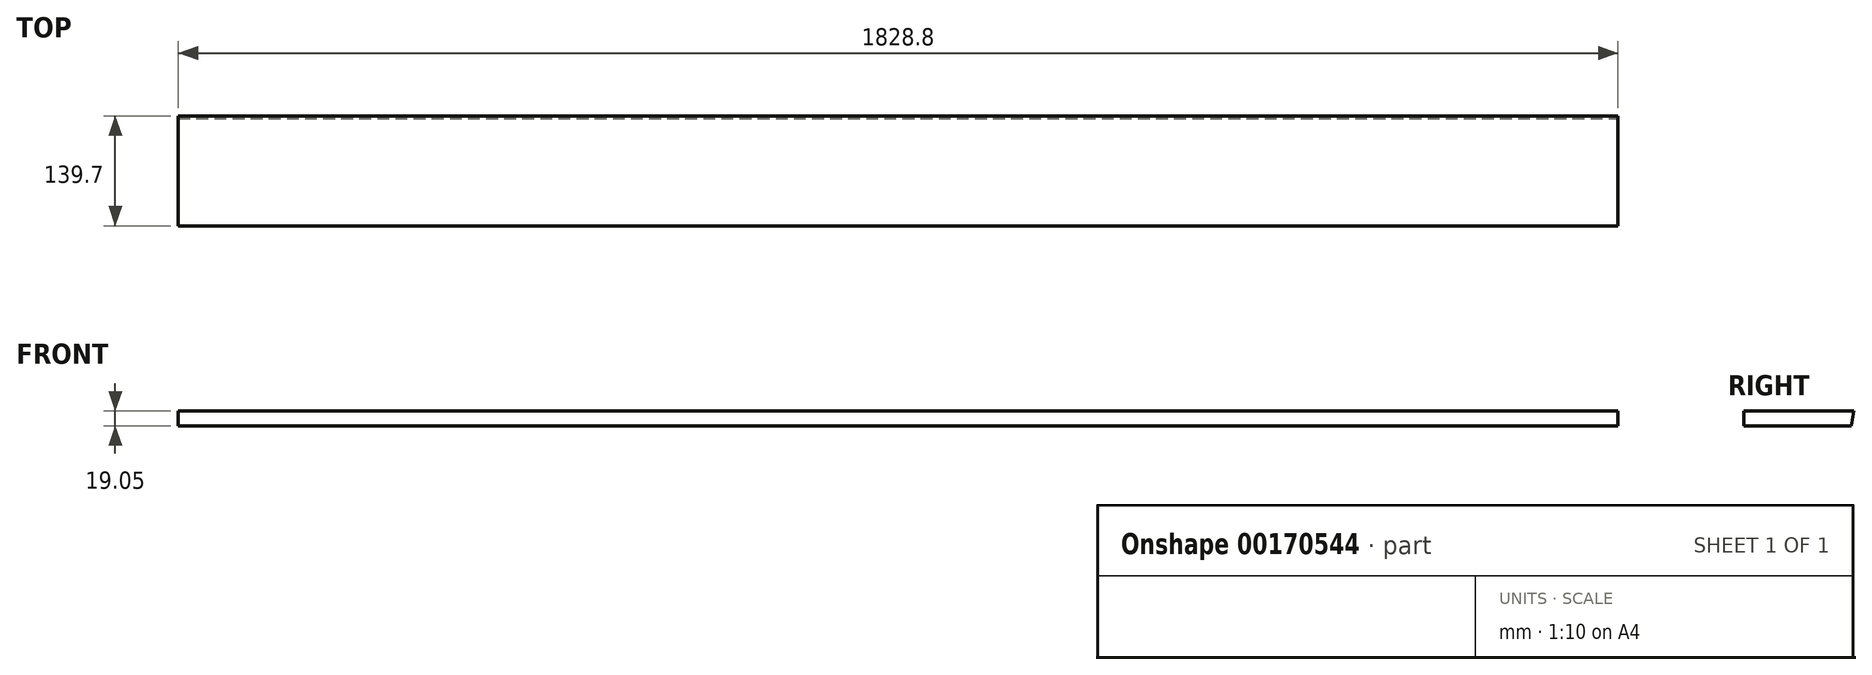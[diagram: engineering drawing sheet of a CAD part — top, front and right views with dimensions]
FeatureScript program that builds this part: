
annotation { "Feature Type Name" : "Feature", "Feature Type Description" : "" }
export const myFeature = defineFeature(function(context is Context, id is Id, definition is map)
    precondition{}
    {
        {
            var Q0;
            Q0=qCreatedBy(makeId("Top.planeOp"),FACE);
            var sketch = newSketch(context, id + "F0", { "sketchPlane" : qUnion([Q0])});
            skLineSegment(sketch, "E0.bottom", {"start": v(0, 0) * mm, "end": v(1828.8, 0) * mm});
            skLineSegment(sketch, "E0.top", {"start": v(0, 139.7) * mm, "end": v(1828.8, 139.7) * mm});
            skLineSegment(sketch, "E0.left", {"start": v(0, 0) * mm, "end": v(0, 139.7) * mm});
            skLineSegment(sketch, "E0.right", {"start": v(1828.8, 0) * mm, "end": v(1828.8, 139.7) * mm});
            skSolve(sketch);
        }
        {
            var Q0;
            Q0=makeQuery(id+"F0.imprint","IMPRINT",FACE,{"disambiguationData":[TD([[makeQuery(id+"F0.imprint","IMPRINT",EDGE,{"derivedFrom":sQuery(id+"F0.wireOp",EDGE,"E0.bottom")}),1.0]])]});
            extrude(context, id + "F1", {"entities" : qUnion([Q0]), "depth" : 19.05 * mm});
        }
        {
            var Q0;
            Q0=makeQuery(id+"F1.opExtrude","SWEPT_FACE",FACE,{"disambiguationData":[OSD([sQuery(id+"F0.wireOp",EDGE,"E0.right")])]});
            var sketch = newSketch(context, id + "F2", { "sketchPlane" : qUnion([Q0])});
            skLineSegment(sketch, "E1", {"start": v(139.7, 19.05) * mm, "end": v(136.34, 0) * mm});
            skSolve(sketch);
        }
        {
            var Q0;
            {var subQ0=sQuery(id+"F2.wireOp",EDGE,"E1");Q0=makeQuery(id+"F2.imprint","IMPRINT",FACE,{"disambiguationData":[TD([[makeQuery(id+"F2.imprint","IMPRINT",EDGE,{"derivedFrom":subQ0}),1.0]])]});}
            extrude(context, id + "F3", {"entities" : qUnion([Q0]), "operationType" : NewBodyOperationType.REMOVE, "endBound" : BoundingType.THROUGH_ALL, "oppositeDirection" : true, "depth" : 25.4 * mm});
        }
    });
